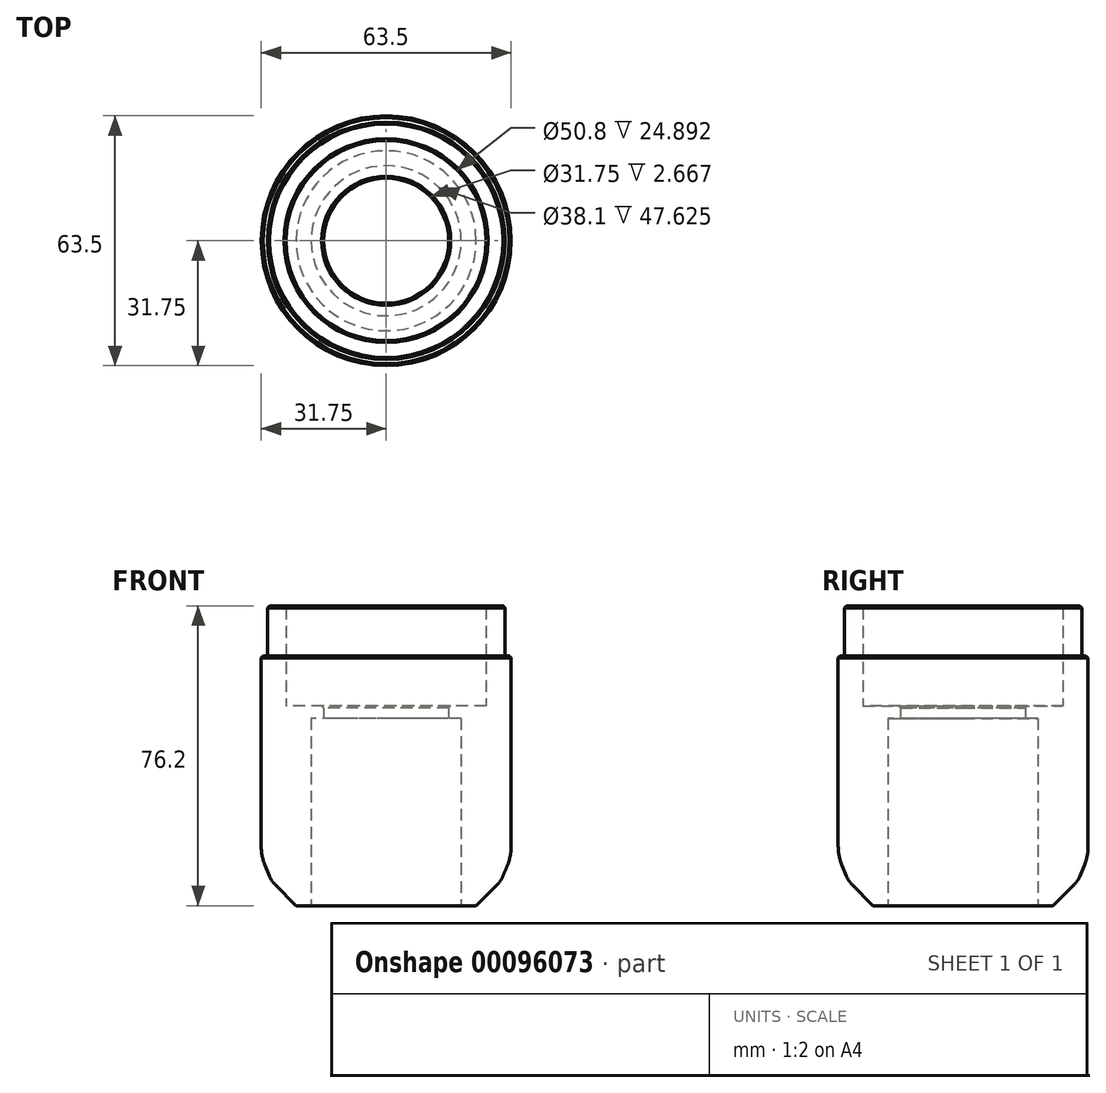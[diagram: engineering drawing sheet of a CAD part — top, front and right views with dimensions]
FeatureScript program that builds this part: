
annotation { "Feature Type Name" : "Feature", "Feature Type Description" : "" }
export const myFeature = defineFeature(function(context is Context, id is Id, definition is map)
    precondition{}
    {
        {
            var Q0;
            Q0=qCreatedBy(makeId("Top.planeOp"),FACE);
            var sketch = newSketch(context, id + "F0", { "sketchPlane" : qUnion([Q0])});
            skCircle(sketch, "E0", {"center": v(0, 0) * mm, "radius": 31.75 * mm});
            skCircle(sketch, "E1", {"center": v(0, 0) * mm, "radius": 30.16 * mm});
            skCircle(sketch, "E2", {"center": v(0, 0) * mm, "radius": 25.4 * mm});
            skCircle(sketch, "E3", {"center": v(0, 0) * mm, "radius": 19.05 * mm});
            skCircle(sketch, "E4", {"center": v(0, 0) * mm, "radius": 15.88 * mm});
            skSolve(sketch);
        }
        {
            var Q0;
            Q0=makeQuery(id+"F0.imprint","IMPRINT",FACE,{"disambiguationData":[TD([[makeQuery(id+"F0.imprint","IMPRINT",EDGE,{"derivedFrom":sQuery(id+"F0.wireOp",EDGE,"E0")}),1.0]])]});
            extrude(context, id + "F1", {"entities" : qUnion([Q0]), "depth" : 63.5 * mm});
        }
        {
            var Q0;
            Q0=makeQuery(id+"F0.imprint","IMPRINT",FACE,{"disambiguationData":[TD([[makeQuery(id+"F0.imprint","IMPRINT",EDGE,{"derivedFrom":sQuery(id+"F0.wireOp",EDGE,"E1")}),1.0]])]});
            extrude(context, id + "F2", {"entities" : qUnion([Q0]), "operationType" : NewBodyOperationType.ADD, "depth" : 76.2 * mm});
        }
        {
            var Q0;
            Q0=makeQuery(id+"F0.imprint","IMPRINT",FACE,{"disambiguationData":[TD([[makeQuery(id+"F0.imprint","IMPRINT",EDGE,{"derivedFrom":sQuery(id+"F0.wireOp",EDGE,"E2")}),1.0]])]});
            extrude(context, id + "F3", {"entities" : qUnion([Q0]), "operationType" : NewBodyOperationType.ADD, "depth" : 50.8 * mm});
        }
        {
            var Q0;
            Q0=makeQuery(id+"F0.imprint","IMPRINT",FACE,{"disambiguationData":[TD([[makeQuery(id+"F0.imprint","IMPRINT",EDGE,{"derivedFrom":sQuery(id+"F0.wireOp",EDGE,"E3")}),1.0]])]});
            extrude(context, id + "F4", {"entities" : qUnion([Q0]), "operationType" : NewBodyOperationType.ADD, "depth" : 50.8 * mm});
        }
        {
            var Q0;
            Q0=makeQuery(id+"F0.imprint","IMPRINT",FACE,{"disambiguationData":[TD([[makeQuery(id+"F0.imprint","IMPRINT",EDGE,{"derivedFrom":sQuery(id+"F0.wireOp",EDGE,"E3")}),1.0]])]});
            extrude(context, id + "F5", {"entities" : qUnion([Q0]), "operationType" : NewBodyOperationType.REMOVE, "depth" : 47.62 * mm});
        }
        {
            var Q0;
            Q0=makeQuery(id+"F1.opExtrude","CAP_FACE",FACE,{"disambiguationData":[OSD([sQuery(id+"F0.wireOp",EDGE,"E0"),sQuery(id+"F0.wireOp",EDGE,"E1")])],"isStart":false});
            cPlane(context, id + "F6", {"entities" : qUnion([Q0]), "cplaneType" : CPlaneType.OFFSET, "offset" : 0 * mm, "width" : 152.4 * mm, "height" : 152.4 * mm});
        }
        {
            var Q0;
            Q0=qCreatedBy(id+"F6.planeOp",FACE);
            var sketch = newSketch(context, id + "F7", { "sketchPlane" : qUnion([Q0])});
            skPoint(sketch, "E5", {"position": v(0, 0) * mm});
            skSolve(sketch);
        }
        {
            var Q0;
            Q0=makeQuery(id+"F5.boolean.opBoolean","COPY",EDGE,{"derivedFrom":makeQuery(id+"F5.opExtrude","CAP_EDGE",EDGE,{"disambiguationData":[OSD([sQuery(id+"F0.wireOp",EDGE,"E3")])],"isStart":true})});
            var Q1;
            Q1=makeQuery(id+"F1.opExtrude","CAP_EDGE",EDGE,{"disambiguationData":[OSD([sQuery(id+"F0.wireOp",EDGE,"E0")])],"isStart":false});
            var Q2;
            Q2=makeQuery(id+"F2.opExtrude","CAP_EDGE",EDGE,{"disambiguationData":[OSD([sQuery(id+"F0.wireOp",EDGE,"E1")])],"isStart":false});
            var Q3;
            Q3=makeQuery(id+"F2.opExtrude","CAP_EDGE",EDGE,{"disambiguationData":[OSD([sQuery(id+"F0.wireOp",EDGE,"E2")])],"isStart":false});
            chamfer(context, id + "F8", {"entities" : qUnion([Q0, Q1, Q2, Q3]), "width" : 0.5 * mm, "tangentPropagation" : true});
        }
        {
            var Q0;
            Q0=makeQuery(id+"F4.opExtrude","CAP_EDGE",EDGE,{"disambiguationData":[OSD([sQuery(id+"F0.wireOp",EDGE,"E4")])],"isStart":false});
            var Q1;
            Q1=makeQuery(id+"F5.boolean.opBoolean","COPY",EDGE,{"derivedFrom":makeQuery(id+"F5.opExtrude","CAP_EDGE",EDGE,{"disambiguationData":[OSD([sQuery(id+"F0.wireOp",EDGE,"E4")])],"isStart":false})});
            chamfer(context, id + "F9", {"entities" : qUnion([Q0, Q1]), "width" : 0.5 * mm, "tangentPropagation" : true});
        }
        {
            var Q0;
            Q0=makeQuery(id+"F1.opExtrude","CAP_EDGE",EDGE,{"disambiguationData":[OSD([sQuery(id+"F0.wireOp",EDGE,"E0")])],"isStart":true});
            chamfer(context, id + "F10", {"entities" : qUnion([Q0]), "width" : 8.9 * mm, "tangentPropagation" : true});
        }
        {
            var Q0;
            {var subQ0=sQuery(id+"F0.wireOp",EDGE,"E0");Q0=makeQuery(id+"F10.opChamfer","BLEND_EDGE",EDGE,{"blendedFrom":[makeQuery(id+"F1.opExtrude","CAP_EDGE",EDGE,{"disambiguationData":[OSD([subQ0])],"isStart":true}),makeQuery(id+"F1.opExtrude","SWEPT_FACE",FACE,{"disambiguationData":[OSD([subQ0])]})],"blendedInto":[makeQuery(id+"F1.opExtrude","SWEPT_FACE",FACE,{"disambiguationData":[OSD([subQ0])]})]});}
            chamfer(context, id + "F11", {"entities" : qUnion([Q0]), "width" : 8.9 * mm, "tangentPropagation" : true});
        }
        {
            var Q0;
            Q0=makeQuery(id+"F5.boolean.opBoolean","COPY",FACE,{"derivedFrom":makeQuery(id+"F5.opExtrude","CAP_FACE",FACE,{"disambiguationData":[OSD([sQuery(id+"F0.wireOp",EDGE,"E3"),sQuery(id+"F0.wireOp",EDGE,"E4")])],"isStart":false})});
            var sketch = newSketch(context, id + "F12", { "sketchPlane" : qUnion([Q0])});
            skPoint(sketch, "E6", {"position": v(0, 0) * mm});
            skPoint(sketch, "E7", {"position": v(45.15, 8.08) * mm});
            skSolve(sketch);
        }
        {
            var Q0;
            {var subQ0=sQuery(id+"F0.wireOp",EDGE,"E0");var subQ1=makeQuery(id+"F1.opExtrude","SWEPT_FACE",FACE,{"disambiguationData":[OSD([subQ0])]});Q0=makeQuery(id+"F11.opChamfer","BLEND_EDGE",EDGE,{"blendedFrom":[makeQuery(id+"F10.opChamfer","BLEND_EDGE",EDGE,{"blendedFrom":[makeQuery(id+"F1.opExtrude","CAP_EDGE",EDGE,{"disambiguationData":[OSD([subQ0])],"isStart":true}),subQ1],"blendedInto":[subQ1]}),subQ1],"blendedInto":[subQ1]});}
            fillet(context, id + "F13", {"entities" : qUnion([Q0]), "radius" : 12.7 * mm, "tangentPropagation" : true, "allowEdgeOverflow" : false});
        }
        {
            var Q0;
            {var subQ0=sQuery(id+"F0.wireOp",EDGE,"E0");Q0=makeQuery(id+"F11.opChamfer","BLEND_EDGE",EDGE,{"blendedFrom":[makeQuery(id+"F10.opChamfer","BLEND_EDGE",EDGE,{"blendedFrom":[makeQuery(id+"F1.opExtrude","CAP_EDGE",EDGE,{"disambiguationData":[OSD([subQ0])],"isStart":true}),makeQuery(id+"F1.opExtrude","SWEPT_FACE",FACE,{"disambiguationData":[OSD([subQ0])]})],"blendedInto":[makeQuery(id+"F1.opExtrude","SWEPT_FACE",FACE,{"disambiguationData":[OSD([subQ0])]})]}),makeQuery(id+"F10.opChamfer","BLEND_FACE",FACE,{"disambiguationData":[OSD([subQ0])]})],"blendedInto":[makeQuery(id+"F10.opChamfer","BLEND_FACE",FACE,{"disambiguationData":[OSD([subQ0])]})]});}
            fillet(context, id + "F14", {"entities" : qUnion([Q0]), "radius" : 6.35 * mm, "tangentPropagation" : true, "allowEdgeOverflow" : false});
        }
    });
